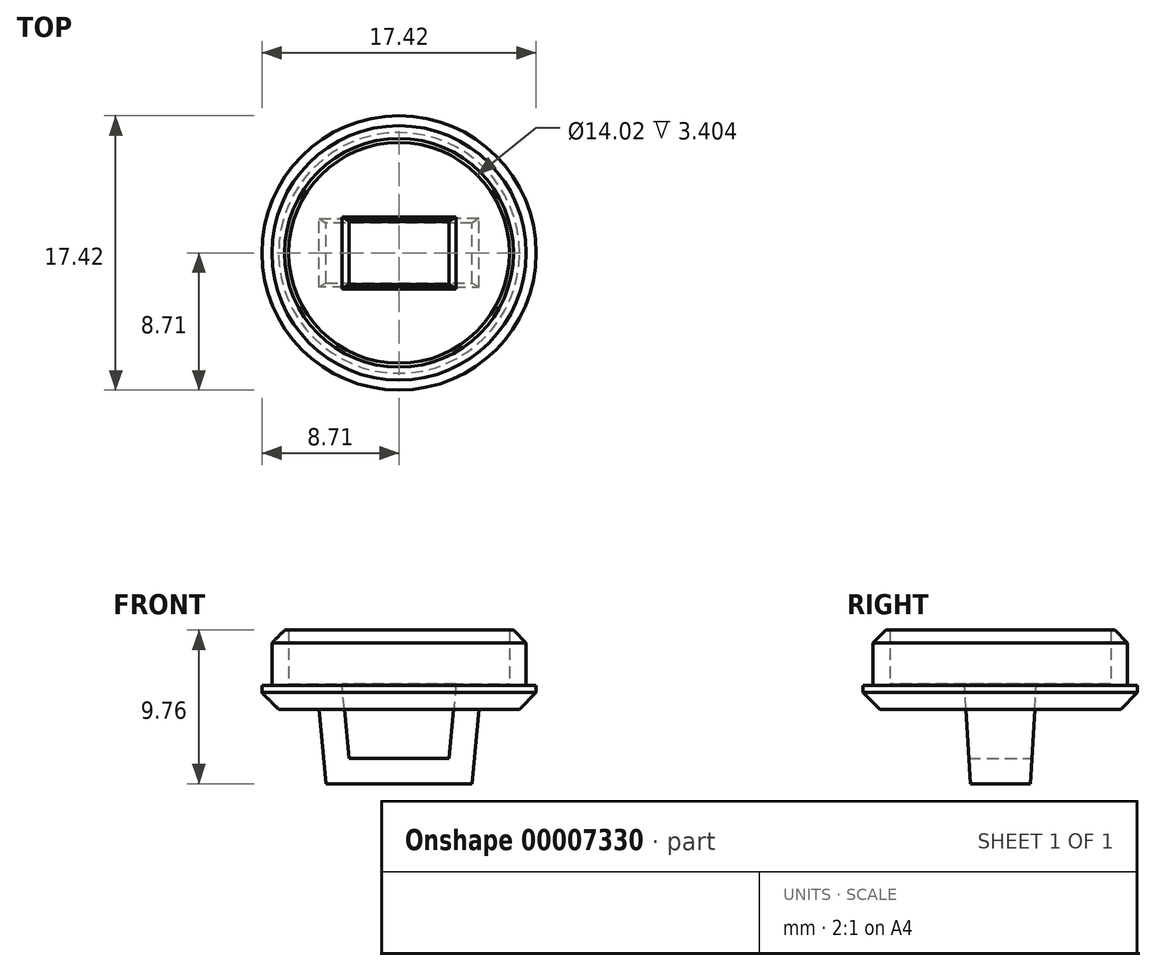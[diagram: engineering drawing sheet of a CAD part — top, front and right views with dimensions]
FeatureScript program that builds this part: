
annotation { "Feature Type Name" : "Feature", "Feature Type Description" : "" }
export const myFeature = defineFeature(function(context is Context, id is Id, definition is map)
    precondition{}
    {
        {
            var Q0;
            Q0=qCreatedBy(makeId("Front.planeOp"),FACE);
            var sketch = newSketch(context, id + "F0", { "sketchPlane" : qUnion([Q0])});
            skLineSegment(sketch, "E0", {"start": v(8.71, 0) * mm, "end": v(8.71, -0.46) * mm});
            skLineSegment(sketch, "E1", {"start": v(8.71, -0.46) * mm, "end": v(7.65, -1.52) * mm});
            skLineSegment(sketch, "E2", {"start": v(7.65, -1.52) * mm, "end": v(0, -1.52) * mm});
            skLineSegment(sketch, "E3", {"start": v(0, -1.52) * mm, "end": v(0, 0) * mm});
            skLineSegment(sketch, "E4", {"start": v(8.08, 0) * mm, "end": v(8.08, 2.7) * mm});
            skLineSegment(sketch, "E5", {"start": v(8.08, 2.7) * mm, "end": v(7.26, 3.5) * mm});
            skLineSegment(sketch, "E6", {"start": v(7.26, 3.5) * mm, "end": v(7.01, 3.5) * mm});
            skLineSegment(sketch, "E7", {"start": v(7.01, 3.5) * mm, "end": v(7.01, 0.1) * mm});
            skLineSegment(sketch, "E8", {"start": v(7.01, 0.1) * mm, "end": v(0, 0.1) * mm});
            skLineSegment(sketch, "E9", {"start": v(8.71, 0) * mm, "end": v(8.08, 0) * mm});
            skLineSegment(sketch, "E10", {"start": v(0, 0.1) * mm, "end": v(0, 0) * mm});
            skSolve(sketch);
        }
        {
            var Q0;
            Q0 = qSketchRegion(id + "F0", true);
            var Q1;
            Q1=sQuery(id+"F0.wireOp",EDGE,"E3");
            revolve(context, id + "F1", {"entities" : qUnion([Q0]), "axis" : qUnion([Q1]), "revolveType" : RevolveType.FULL});
        }
        {
            var Q0;
            Q0=qCreatedBy(makeId("Right.planeOp"),FACE);
            var sketch = newSketch(context, id + "F2", { "sketchPlane" : qUnion([Q0])});
            skLineSegment(sketch, "E11", {"start": v(0, 0) * mm, "end": v(0, -6.25) * mm});
            skLineSegment(sketch, "E12", {"start": v(0, -6.25) * mm, "end": v(1.9, -6.25) * mm, "construction": true});
            skLineSegment(sketch, "E13", {"start": v(1.9, -6.25) * mm, "end": v(2.48, 3.5) * mm});
            skLineSegment(sketch, "E14", {"start": v(2.48, 3.5) * mm, "end": v(0, 3.5) * mm});
            skLineSegment(sketch, "E15", {"start": v(0, 3.5) * mm, "end": v(0, 0) * mm});
            skPoint(sketch, "E16", {"position": v(2.18, -1.52) * mm});
            skLineSegment(sketch, "E17", {"start": v(0, -4.65) * mm, "end": v(2, -4.65) * mm});
            skLineSegment(sketch, "E18.0.MirrorCS", {"start": v(0, -4.65) * mm, "end": v(-2, -4.65) * mm});
            skLineSegment(sketch, "E19.0.MirrorCS", {"start": v(0, -6.25) * mm, "end": v(-1.9, -6.25) * mm, "construction": true});
            skLineSegment(sketch, "E20.0.MirrorCS", {"start": v(-1.9, -6.25) * mm, "end": v(-2.48, 3.5) * mm});
            skLineSegment(sketch, "E21.0.MirrorCS", {"start": v(-2.48, 3.5) * mm, "end": v(0, 3.5) * mm});
            skSolve(sketch);
        }
        {
            var Q0;
            Q0=qCreatedBy(makeId("Front.planeOp"),FACE);
            var sketch = newSketch(context, id + "F3", { "sketchPlane" : qUnion([Q0])});
            skLineSegment(sketch, "E22", {"start": v(0, 0) * mm, "end": v(0, 3.5) * mm});
            skLineSegment(sketch, "E23", {"start": v(0, 3.5) * mm, "end": v(5.54, 3.5) * mm, "construction": true});
            skLineSegment(sketch, "E24", {"start": v(5.54, 3.5) * mm, "end": v(4.65, -6.25) * mm});
            skLineSegment(sketch, "E25", {"start": v(4.65, -6.25) * mm, "end": v(0, -6.25) * mm});
            skLineSegment(sketch, "E26", {"start": v(0, -6.25) * mm, "end": v(0, 0) * mm});
            skLineSegment(sketch, "E27", {"start": v(0, -4.65) * mm, "end": v(3.19, -4.65) * mm});
            skLineSegment(sketch, "E28", {"start": v(3.19, -4.65) * mm, "end": v(3.93, 3.5) * mm});
            skPoint(sketch, "E29", {"position": v(5.08, -1.52) * mm});
            skLineSegment(sketch, "E30", {"start": v(5.08, -1.52) * mm, "end": v(3.47, -1.52) * mm});
            skLineSegment(sketch, "E31.0.MirrorCS", {"start": v(-3.19, -4.65) * mm, "end": v(-3.93, 3.5) * mm});
            skLineSegment(sketch, "E32.0.MirrorCS", {"start": v(-5.54, 3.5) * mm, "end": v(-4.65, -6.25) * mm});
            skLineSegment(sketch, "E33.0.MirrorCS", {"start": v(0, -4.65) * mm, "end": v(-3.19, -4.65) * mm});
            skLineSegment(sketch, "E34.0.MirrorCS", {"start": v(-4.65, -6.25) * mm, "end": v(0, -6.25) * mm});
            skLineSegment(sketch, "E35.0.MirrorCS", {"start": v(-5.08, -1.52) * mm, "end": v(-3.47, -1.52) * mm});
            skSolve(sketch);
        }
        {
            var Q0;
            Q0=sQuery(id+"F3.wireOp",VERTEX,"E34.0.MirrorCS.end");
            var Q1;
            Q1=sQuery(id+"F3.wireOp",VERTEX,"E25.start");
            var Q2;
            Q2=sQuery(id+"F2.wireOp",VERTEX,"E20.0.MirrorCS.start");
            cPlane(context, id + "F4", {"entities" : qUnion([Q0, Q1, Q2]), "cplaneType" : CPlaneType.THREE_POINT, "offset" : 152.4 * mm, "width" : 152.4 * mm, "height" : 152.4 * mm});
        }
        {
            var Q0;
            Q0=qCreatedBy(id+"F4.planeOp",FACE);
            var sketch = newSketch(context, id + "F5", { "sketchPlane" : qUnion([Q0])});
            skLineSegment(sketch, "E36", {"start": v(4.65, 0) * mm, "end": v(4.65, -1.9) * mm});
            skLineSegment(sketch, "E37", {"start": v(4.65, -1.9) * mm, "end": v(0, -1.9) * mm});
            skLineSegment(sketch, "E38.0", {"start": v(0, 0) * mm, "end": v(0, -1.9) * mm, "construction": true});
            skLineSegment(sketch, "E39.0.MirrorCS", {"start": v(-4.65, 0) * mm, "end": v(-4.65, -1.9) * mm});
            skLineSegment(sketch, "E40.0.MirrorCS", {"start": v(-4.65, -1.9) * mm, "end": v(0, -1.9) * mm});
            skLineSegment(sketch, "E41.0", {"start": v(4.65, 0) * mm, "end": v(0, 0) * mm, "construction": true});
            skLineSegment(sketch, "E42", {"start": v(-4.65, 0) * mm, "end": v(4.65, 0) * mm});
            skLineSegment(sketch, "E43.0.MirrorCS", {"start": v(4.65, 0) * mm, "end": v(4.65, 1.9) * mm});
            skLineSegment(sketch, "E44.0.MirrorCS", {"start": v(4.65, 1.9) * mm, "end": v(0, 1.9) * mm});
            skLineSegment(sketch, "E45.0.MirrorCS", {"start": v(-4.65, 1.9) * mm, "end": v(0, 1.9) * mm});
            skLineSegment(sketch, "E46.0.MirrorCS", {"start": v(-4.65, 0) * mm, "end": v(-4.65, 1.9) * mm});
            skSolve(sketch);
        }
        {
            var Q0;
            Q0=sQuery(id+"F2.wireOp",VERTEX,"E20.0.MirrorCS.end");
            var Q1;
            Q1=sQuery(id+"F5.wireOp",VERTEX,"E40.0.MirrorCS.start");
            var Q2;
            Q2=sQuery(id+"F5.wireOp",VERTEX,"E36.end");
            cPlane(context, id + "F6", {"entities" : qUnion([Q0, Q1, Q2]), "cplaneType" : CPlaneType.THREE_POINT, "offset" : 152.4 * mm, "width" : 152.4 * mm, "height" : 152.4 * mm});
        }
        {
            var Q0;
            Q0=sQuery(id+"F2.wireOp",VERTEX,"E14.start");
            var Q1;
            Q1=sQuery(id+"F5.wireOp",VERTEX,"E45.0.MirrorCS.start");
            var Q2;
            Q2=sQuery(id+"F5.wireOp",VERTEX,"E43.0.MirrorCS.end");
            cPlane(context, id + "F7", {"entities" : qUnion([Q0, Q1, Q2]), "cplaneType" : CPlaneType.THREE_POINT, "offset" : 152.4 * mm, "width" : 152.4 * mm, "height" : 152.4 * mm});
        }
        {
            var Q0;
            Q0 = qSketchRegion(id + "F3", true);
            var Q1;
            Q1=qCreatedBy(id+"F6.planeOp",FACE);
            extrude(context, id + "F8", {"entities" : qUnion([Q0]), "operationType" : NewBodyOperationType.ADD, "endBound" : BoundingType.UP_TO_SURFACE, "endBoundEntityFace" : qUnion([Q1]), "depth" : 25.4 * mm});
        }
        {
            var Q0;
            Q0 = qSketchRegion(id + "F3", true);
            var Q1;
            Q1=qCreatedBy(id+"F7.planeOp",FACE);
            extrude(context, id + "F9", {"entities" : qUnion([Q0]), "operationType" : NewBodyOperationType.ADD, "endBound" : BoundingType.UP_TO_SURFACE, "oppositeDirection" : true, "endBoundEntityFace" : qUnion([Q1]), "depth" : 25.4 * mm});
        }
        {
            var Q0;
            Q0 = qSketchRegion(id + "F2", true);
            var Q1;
            {var subQ0=sQuery(id+"F3.wireOp",EDGE,"E31.0.MirrorCS");Q1=makeQuery(id+"F9.boolean.opBoolean","MERGE",FACE,{"derivedFrom":[makeQuery(id+"F8.opExtrude","SWEPT_FACE",FACE,{"disambiguationData":[OSD([subQ0])]}),makeQuery(id+"F9.opExtrude","SWEPT_FACE",FACE,{"disambiguationData":[OSD([subQ0])]})]});}
            extrude(context, id + "F10", {"entities" : qUnion([Q0]), "operationType" : NewBodyOperationType.REMOVE, "endBound" : BoundingType.UP_TO_SURFACE, "oppositeDirection" : true, "endBoundEntityFace" : qUnion([Q1]), "depth" : 25.4 * mm});
        }
        {
            var Q0;
            Q0 = qSketchRegion(id + "F2", true);
            var Q1;
            {var subQ0=sQuery(id+"F3.wireOp",EDGE,"E28");Q1=makeQuery(id+"F9.boolean.opBoolean","MERGE",FACE,{"derivedFrom":[makeQuery(id+"F8.opExtrude","SWEPT_FACE",FACE,{"disambiguationData":[OSD([subQ0])]}),makeQuery(id+"F9.opExtrude","SWEPT_FACE",FACE,{"disambiguationData":[OSD([subQ0])]})]});}
            extrude(context, id + "F11", {"entities" : qUnion([Q0]), "operationType" : NewBodyOperationType.REMOVE, "endBound" : BoundingType.UP_TO_SURFACE, "endBoundEntityFace" : qUnion([Q1]), "depth" : 25.4 * mm});
        }
    });
